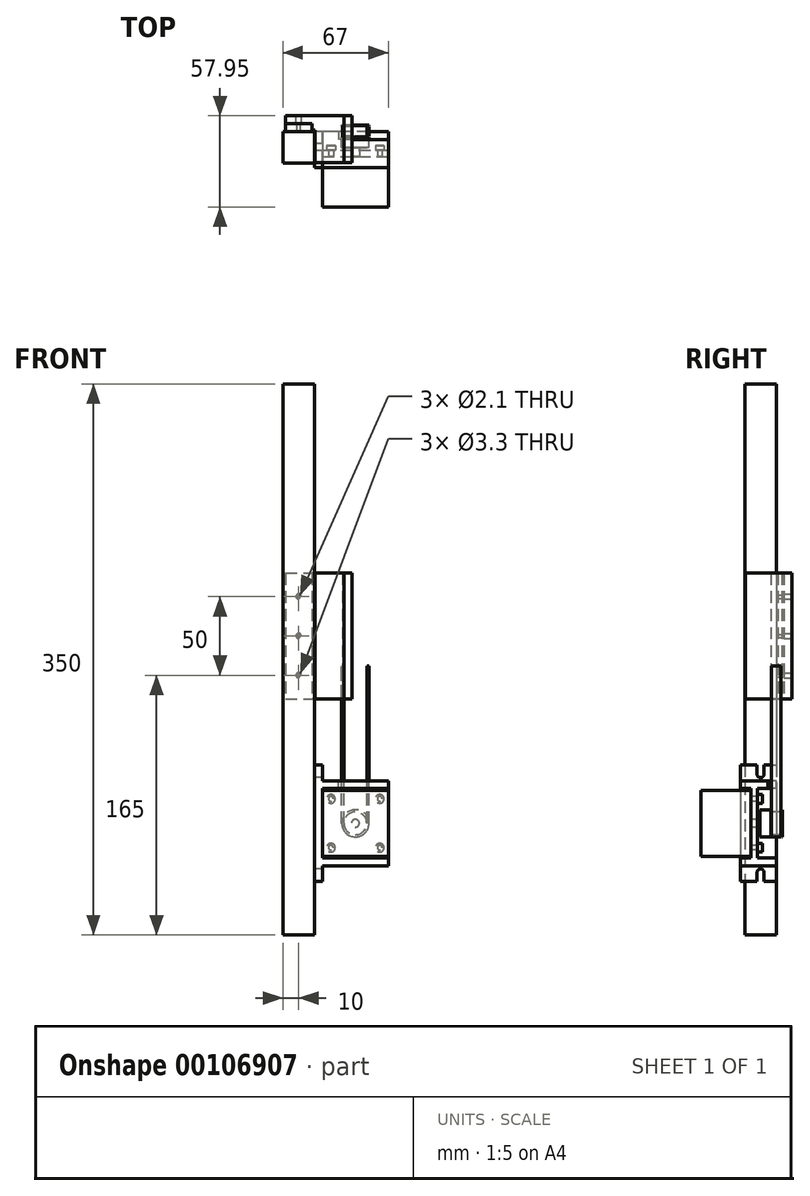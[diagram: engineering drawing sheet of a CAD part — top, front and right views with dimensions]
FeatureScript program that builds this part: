
annotation { "Feature Type Name" : "Feature", "Feature Type Description" : "" }
export const myFeature = defineFeature(function(context is Context, id is Id, definition is map)
    precondition{}
    {
        {
            var Q0;
            Q0=qCreatedBy(makeId("Top.planeOp"),FACE);
            var sketch = newSketch(context, id + "F0", { "sketchPlane" : qUnion([Q0])});
            skLineSegment(sketch, "E0.bottom", {"start": v(10, -10) * mm, "end": v(-10, -10) * mm, "construction": true});
            skLineSegment(sketch, "E0.top", {"start": v(10, 10) * mm, "end": v(-10, 10) * mm, "construction": true});
            skLineSegment(sketch, "E0.left", {"start": v(10, -10) * mm, "end": v(10, 10) * mm, "construction": true});
            skLineSegment(sketch, "E0.right", {"start": v(-10, -10) * mm, "end": v(-10, 10) * mm, "construction": true});
            skPoint(sketch, "E0.middle", {"position": v(0, 0) * mm});
            skLineSegment(sketch, "E1.bottom", {"start": v(15, -5.95) * mm, "end": v(57, -5.95) * mm, "construction": true});
            skLineSegment(sketch, "E1.top", {"start": v(15, -37.95) * mm, "end": v(57, -37.95) * mm, "construction": true});
            skLineSegment(sketch, "E1.left", {"start": v(15, -5.95) * mm, "end": v(15, -37.95) * mm, "construction": true});
            skLineSegment(sketch, "E1.right", {"start": v(57, -5.95) * mm, "end": v(57, -37.95) * mm, "construction": true});
            skLineSegment(sketch, "E2.bottom", {"start": v(33.5, -5.95) * mm, "end": v(38.5, -5.95) * mm, "construction": true});
            skLineSegment(sketch, "E2.top", {"start": v(33.5, 14.05) * mm, "end": v(38.5, 14.05) * mm, "construction": true});
            skLineSegment(sketch, "E2.left", {"start": v(33.5, -5.95) * mm, "end": v(33.5, 14.05) * mm, "construction": true});
            skLineSegment(sketch, "E2.right", {"start": v(38.5, -5.95) * mm, "end": v(38.5, 14.05) * mm, "construction": true});
            skPoint(sketch, "E2.middle", {"position": v(36, 4.05) * mm});
            skPoint(sketch, "E2.middle.positionSnap0", {"position": v(36, -5.95) * mm});
            skPoint(sketch, "E2.centerSnap0", {"position": v(36, -5.95) * mm});
            skLineSegment(sketch, "E3.top", {"start": v(44.65, -0.25) * mm, "end": v(27.35, -0.25) * mm, "construction": true});
            skLineSegment(sketch, "E3.left", {"start": v(44.65, 14.05) * mm, "end": v(44.65, -0.25) * mm, "construction": true});
            skPoint(sketch, "E3.middle", {"position": v(36, 6.9) * mm});
            skPoint(sketch, "E3.middle.positionSnap0", {"position": v(36, 14.05) * mm});
            skPoint(sketch, "E3.cornerSnap0", {"position": v(36, 14.05) * mm});
            skPoint(sketch, "E3.centerSnap0", {"position": v(36, 14.05) * mm});
            skLineSegment(sketch, "E4.bottom", {"start": v(-8.5, 10) * mm, "end": v(8.5, 10) * mm, "construction": true});
            skLineSegment(sketch, "E4.top", {"start": v(-8.5, 15) * mm, "end": v(8.5, 15) * mm, "construction": true});
            skLineSegment(sketch, "E4.left", {"start": v(-8.5, 10) * mm, "end": v(-8.5, 15) * mm, "construction": true});
            skLineSegment(sketch, "E4.right", {"start": v(8.5, 10) * mm, "end": v(8.5, 15) * mm, "construction": true});
            skPoint(sketch, "E4.middle", {"position": v(0, 12.5) * mm});
            skPoint(sketch, "E4.middle.positionSnap0", {"position": v(0, 10) * mm});
            skPoint(sketch, "E4.centerSnap0", {"position": v(0, 10) * mm});
            skLineSegment(sketch, "E5.bottom", {"start": v(10, 10) * mm, "end": v(15, 10) * mm, "construction": true});
            skLineSegment(sketch, "E5.top", {"start": v(10, -12.85) * mm, "end": v(15, -12.85) * mm, "construction": true});
            skLineSegment(sketch, "E5.left", {"start": v(10, 10) * mm, "end": v(10, -12.85) * mm, "construction": true});
            skLineSegment(sketch, "E5.right", {"start": v(15, 10) * mm, "end": v(15, -1.95) * mm, "construction": true});
            skLineSegment(sketch, "E6.bottom", {"start": v(15, -1.95) * mm, "end": v(57, -1.95) * mm, "construction": true});
            skLineSegment(sketch, "E6.right", {"start": v(57, -1.95) * mm, "end": v(57, -5.95) * mm, "construction": true});
            skLineSegment(sketch, "E7.trimOffspring", {"start": v(15, -5.95) * mm, "end": v(15, -12.85) * mm, "construction": true});
            skLineSegment(sketch, "E8", {"start": v(27.35, -0.25) * mm, "end": v(27.35, 14.05) * mm, "construction": true});
            skLineSegment(sketch, "E9", {"start": v(27.35, 14.05) * mm, "end": v(44.65, 14.05) * mm, "construction": true});
            skPoint(sketch, "E10", {"position": v(27.35, 6.9) * mm});
            skSolve(sketch);
        }
        {
            var Q0;
            Q0=qCreatedBy(makeId("Top.planeOp"),FACE);
            var sketch = newSketch(context, id + "F1", { "sketchPlane" : qUnion([Q0])});
            skLineSegment(sketch, "E11.0", {"start": v(10, -10) * mm, "end": v(-10, -10) * mm});
            skLineSegment(sketch, "E12.0", {"start": v(-10, -10) * mm, "end": v(-10, 10) * mm});
            skLineSegment(sketch, "E13.0", {"start": v(10, -10) * mm, "end": v(10, 10) * mm});
            skLineSegment(sketch, "E14.0", {"start": v(10, 10) * mm, "end": v(-10, 10) * mm});
            skSolve(sketch);
        }
        {
            var Q0;
            Q0 = qSketchRegion(id + "F1", true);
            extrude(context, id + "F2", {"entities" : qUnion([Q0]), "depth" : 300 * mm, "hasSecondDirection" : true, "secondDirectionOppositeDirection" : true, "secondDirectionDepth" : 50 * mm});
        }
        {
            var Q0;
            Q0=qCreatedBy(makeId("Top.planeOp"),FACE);
            var sketch = newSketch(context, id + "F3", { "sketchPlane" : qUnion([Q0])});
            skLineSegment(sketch, "E15.0", {"start": v(15, -5.95) * mm, "end": v(15, -37.95) * mm});
            skLineSegment(sketch, "E16.0", {"start": v(15, -5.95) * mm, "end": v(57, -5.95) * mm});
            skLineSegment(sketch, "E17.0", {"start": v(57, -5.95) * mm, "end": v(57, -37.95) * mm});
            skLineSegment(sketch, "E18.0", {"start": v(15, -37.95) * mm, "end": v(57, -37.95) * mm});
            skSolve(sketch);
        }
        {
            var Q0;
            Q0 = qSketchRegion(id + "F3", true);
            extrude(context, id + "F4", {"entities" : qUnion([Q0]), "depth" : 42 * mm});
        }
        {
            var Q0;
            Q0=makeQuery(id+"F4.opExtrude","SWEPT_FACE",FACE,{"disambiguationData":[OSD([sQuery(id+"F3.wireOp",EDGE,"E16.0")])]});
            var sketch = newSketch(context, id + "F5", { "sketchPlane" : qUnion([Q0])});
            skCircle(sketch, "E19", {"center": v(-36, 21) * mm, "radius": 2.5 * mm});
            skPoint(sketch, "E19.centerSnap0", {"position": v(-36, 42) * mm});
            skPoint(sketch, "E19.centerSnap1", {"position": v(-57, 21) * mm});
            skSolve(sketch);
        }
        {
            var Q0;
            Q0 = qSketchRegion(id + "F5", true);
            extrude(context, id + "F6", {"entities" : qUnion([Q0]), "operationType" : NewBodyOperationType.ADD, "depth" : 20 * mm});
        }
        {
            var Q0;
            Q0=makeQuery(id+"F6.opExtrude","CAP_FACE",FACE,{"disambiguationData":[OSD([sQuery(id+"F5.wireOp",EDGE,"E19")])],"isStart":false});
            var sketch = newSketch(context, id + "F7", { "sketchPlane" : qUnion([Q0])});
            skCircle(sketch, "E20", {"center": v(-36, 21) * mm, "radius": 8.65 * mm});
            skSolve(sketch);
        }
        {
            var Q0;
            Q0 = qSketchRegion(id + "F7", true);
            extrude(context, id + "F8", {"entities" : qUnion([Q0]), "operationType" : NewBodyOperationType.ADD, "oppositeDirection" : true, "depth" : 14.3 * mm});
        }
        {
            var Q0;
            Q0=makeQuery(id+"F4.opExtrude","SWEPT_FACE",FACE,{"disambiguationData":[OSD([sQuery(id+"F3.wireOp",EDGE,"E16.0")])]});
            var sketch = newSketch(context, id + "F9", { "sketchPlane" : qUnion([Q0])});
            skCircle(sketch, "E21.0", {"center": v(-36, 21) * mm, "radius": 2.5 * mm, "construction": true});
            skLineSegment(sketch, "E22.bottom", {"start": v(-20.5, 5.5) * mm, "end": v(-51.5, 5.5) * mm, "construction": true});
            skLineSegment(sketch, "E22.top", {"start": v(-20.5, 36.5) * mm, "end": v(-51.5, 36.5) * mm, "construction": true});
            skLineSegment(sketch, "E22.left", {"start": v(-20.5, 5.5) * mm, "end": v(-20.5, 36.5) * mm, "construction": true});
            skLineSegment(sketch, "E22.right", {"start": v(-51.5, 5.5) * mm, "end": v(-51.5, 36.5) * mm, "construction": true});
            skCircle(sketch, "E23", {"center": v(-51.5, 36.5) * mm, "radius": 1.5 * mm});
            skCircle(sketch, "E24.0.1.0", {"center": v(-51.5, 5.5) * mm, "radius": 1.5 * mm});
            skCircle(sketch, "E24.1.0.0", {"center": v(-20.5, 36.5) * mm, "radius": 1.5 * mm});
            skCircle(sketch, "E24.1.1.0", {"center": v(-20.5, 5.5) * mm, "radius": 1.5 * mm});
            skLineSegment(sketch, "E24.direction1", {"start": v(-51.5, 36.5) * mm, "end": v(-20.5, 36.5) * mm, "construction": true});
            skLineSegment(sketch, "E24.direction2", {"start": v(-51.5, 36.5) * mm, "end": v(-51.5, 5.5) * mm, "construction": true});
            skSolve(sketch);
        }
        {
            var Q0;
            Q0 = qSketchRegion(id + "F9", true);
            extrude(context, id + "F10", {"entities" : qUnion([Q0]), "operationType" : NewBodyOperationType.ADD, "depth" : 4 * mm});
        }
        {
            var Q0;
            Q0=makeQuery(id+"F10.opExtrude","CAP_FACE",FACE,{"disambiguationData":[OSD([sQuery(id+"F9.wireOp",EDGE,"E24.1.0.0")])],"isStart":false});
            var sketch = newSketch(context, id + "F11", { "sketchPlane" : qUnion([Q0])});
            skCircle(sketch, "E25", {"center": v(-20.5, 36.5) * mm, "radius": 2.75 * mm});
            skCircle(sketch, "E26.0.1.0", {"center": v(-20.5, 5.5) * mm, "radius": 2.75 * mm});
            skCircle(sketch, "E26.1.0.0", {"center": v(-51.5, 36.5) * mm, "radius": 2.75 * mm});
            skCircle(sketch, "E26.1.1.0", {"center": v(-51.5, 5.5) * mm, "radius": 2.75 * mm});
            skLineSegment(sketch, "E26.direction1", {"start": v(-20.5, 36.5) * mm, "end": v(-51.5, 36.5) * mm, "construction": true});
            skLineSegment(sketch, "E26.direction2", {"start": v(-20.5, 36.5) * mm, "end": v(-20.5, 5.5) * mm, "construction": true});
            skSolve(sketch);
        }
        {
            var Q0;
            Q0 = qSketchRegion(id + "F11", true);
            extrude(context, id + "F12", {"entities" : qUnion([Q0]), "operationType" : NewBodyOperationType.ADD, "depth" : 3 * mm});
        }
        {
            var Q0;
            Q0=qCreatedBy(makeId("Top.planeOp"),FACE);
            var sketch = newSketch(context, id + "F13", { "sketchPlane" : qUnion([Q0])});
            skLineSegment(sketch, "E27.0", {"start": v(15, -1.95) * mm, "end": v(57, -1.95) * mm});
            skLineSegment(sketch, "E28.0", {"start": v(57, -1.95) * mm, "end": v(57, -5.95) * mm});
            skLineSegment(sketch, "E29.0", {"start": v(15, -5.95) * mm, "end": v(57, -5.95) * mm});
            skLineSegment(sketch, "E30.0", {"start": v(15, 10) * mm, "end": v(15, -1.95) * mm});
            skLineSegment(sketch, "E31.0", {"start": v(10, 10) * mm, "end": v(15, 10) * mm});
            skLineSegment(sketch, "E32.0", {"start": v(10, 10) * mm, "end": v(10, -12.85) * mm});
            skLineSegment(sketch, "E33.0", {"start": v(10, -12.85) * mm, "end": v(15, -12.85) * mm});
            skLineSegment(sketch, "E34.0", {"start": v(15, 4.05) * mm, "end": v(15, -1.95) * mm});
            skLineSegment(sketch, "E35", {"start": v(15, -5.95) * mm, "end": v(15, -12.85) * mm});
            skSolve(sketch);
        }
        {
            var Q0;
            Q0 = qSketchRegion(id + "F13", true);
            extrude(context, id + "F14", {"entities" : qUnion([Q0]), "depth" : 43 * mm, "hasSecondDirection" : true, "secondDirectionOppositeDirection" : true, "secondDirectionDepth" : 1 * mm});
        }
        {
            var Q0;
            Q0=makeQuery(id+"F14.opExtrude","SWEPT_FACE",FACE,{"disambiguationData":[OSD([sQuery(id+"F13.wireOp",EDGE,"E32.0")])]});
            var sketch = newSketch(context, id + "F15", { "sketchPlane" : qUnion([Q0])});
            skLineSegment(sketch, "E36.bottom", {"start": v(12.85, 43) * mm, "end": v(-10, 43) * mm});
            skLineSegment(sketch, "E36.top", {"start": v(12.85, 58) * mm, "end": v(2.2, 58) * mm});
            skLineSegment(sketch, "E36.left", {"start": v(12.85, 43) * mm, "end": v(12.85, 58) * mm});
            skLineSegment(sketch, "E36.right", {"start": v(-10, 43) * mm, "end": v(-10, 58) * mm});
            skArc(sketch, "E37", {"start": v(-2.2, 52.2) * mm, "mid": v(0, 50) * mm, "end": v(2.2, 52.2) * mm});
            skPoint(sketch, "E37.centerSnap0", {"position": v(0, 58) * mm});
            skLineSegment(sketch, "E38", {"start": v(2.2, 52.2) * mm, "end": v(2.2, 58) * mm});
            skLineSegment(sketch, "E39", {"start": v(-2.2, 52.2) * mm, "end": v(-2.2, 58) * mm});
            skLineSegment(sketch, "E40.trimOffspring", {"start": v(-2.2, 58) * mm, "end": v(-10, 58) * mm});
            skPoint(sketch, "E41", {"position": v(0, 50) * mm});
            skLineSegment(sketch, "E42", {"start": v(-10, 21) * mm, "end": v(-15.85, 21) * mm, "construction": true});
            skLineSegment(sketch, "E43.MirrorCS", {"start": v(-2.2, -10.2) * mm, "end": v(-2.2, -16) * mm});
            skLineSegment(sketch, "E44.MirrorCS", {"start": v(-2.2, -16) * mm, "end": v(-10, -16) * mm});
            skArc(sketch, "E45.MirrorCS", {"start": v(-2.2, -10.2) * mm, "mid": v(0, -8) * mm, "end": v(2.2, -10.2) * mm});
            skLineSegment(sketch, "E46.MirrorCS", {"start": v(12.85, -1) * mm, "end": v(-10, -1) * mm});
            skLineSegment(sketch, "E47.MirrorCS", {"start": v(12.85, -16) * mm, "end": v(2.2, -16) * mm});
            skLineSegment(sketch, "E48.MirrorCS", {"start": v(2.2, -10.2) * mm, "end": v(2.2, -16) * mm});
            skPoint(sketch, "E49.MirrorP", {"position": v(0, -8) * mm});
            skLineSegment(sketch, "E50.MirrorCS", {"start": v(12.85, -1) * mm, "end": v(12.85, -16) * mm});
            skPoint(sketch, "E51.MirrorP", {"position": v(0, -16) * mm});
            skLineSegment(sketch, "E52.MirrorCS", {"start": v(-10, -1) * mm, "end": v(-10, -16) * mm});
            skSolve(sketch);
        }
        {
            var Q0;
            Q0 = qSketchRegion(id + "F15", true);
            var Q1;
            Q1=makeQuery(id+"F14.opExtrude","SWEPT_FACE",FACE,{"disambiguationData":[OSD([sQuery(id+"F13.wireOp",EDGE,"E30.0")])]});
            extrude(context, id + "F16", {"entities" : qUnion([Q0]), "operationType" : NewBodyOperationType.ADD, "endBound" : BoundingType.UP_TO_SURFACE, "oppositeDirection" : true, "endBoundEntityFace" : qUnion([Q1]), "depth" : 25 * mm});
        }
        {
            var Q0;
            {var subQ0=sQuery(id+"F13.wireOp",EDGE,"E30.0");Q0=makeQuery(id+"F16.boolean.opBoolean","MERGE",FACE,{"derivedFrom":[makeQuery(id+"F14.opExtrude","SWEPT_FACE",FACE,{"disambiguationData":[OSD([subQ0])]}),makeQuery(id+"F14.opExtrude","SWEPT_FACE",FACE,{"disambiguationData":[OSD([sQuery(id+"F13.wireOp",EDGE,"E34.0")])]}),makeQuery(id+"F16.opExtrude","CAP_FACE",FACE,{"disambiguationData":[OSD([subQ0]),ownerDisambiguation([makeQuery(id+"F16.opExtrude","SWEPT_BODY",BODY,{"disambiguationData":[OSD([sQuery(id+"F15.wireOp",EDGE,"E36.bottom"),sQuery(id+"F15.wireOp",EDGE,"E36.top"),sQuery(id+"F15.wireOp",EDGE,"E36.left"),sQuery(id+"F15.wireOp",EDGE,"E36.right"),sQuery(id+"F15.wireOp",EDGE,"E37"),sQuery(id+"F15.wireOp",EDGE,"E38"),sQuery(id+"F15.wireOp",EDGE,"E39"),sQuery(id+"F15.wireOp",EDGE,"E40.trimOffspring")])]})])],"isStart":false}),makeQuery(id+"F16.opExtrude","CAP_FACE",FACE,{"disambiguationData":[OSD([subQ0]),ownerDisambiguation([makeQuery(id+"F16.opExtrude","SWEPT_BODY",BODY,{"disambiguationData":[OSD([sQuery(id+"F15.wireOp",EDGE,"E43.MirrorCS"),sQuery(id+"F15.wireOp",EDGE,"E44.MirrorCS"),sQuery(id+"F15.wireOp",EDGE,"E45.MirrorCS"),sQuery(id+"F15.wireOp",EDGE,"E46.MirrorCS"),sQuery(id+"F15.wireOp",EDGE,"E47.MirrorCS"),sQuery(id+"F15.wireOp",EDGE,"E48.MirrorCS"),sQuery(id+"F15.wireOp",EDGE,"E50.MirrorCS"),sQuery(id+"F15.wireOp",EDGE,"E52.MirrorCS")])]})])],"isStart":false})]});}
            var sketch = newSketch(context, id + "F17", { "sketchPlane" : qUnion([Q0])});
            skLineSegment(sketch, "E53.bottom", {"start": v(10, 43) * mm, "end": v(-12.85, 43) * mm});
            skLineSegment(sketch, "E53.top", {"start": v(10, 48) * mm, "end": v(-12.85, 48) * mm});
            skLineSegment(sketch, "E53.left", {"start": v(10, 43) * mm, "end": v(10, 48) * mm});
            skLineSegment(sketch, "E53.right", {"start": v(-12.85, 43) * mm, "end": v(-12.85, 48) * mm});
            skLineSegment(sketch, "E54", {"start": v(10, 21) * mm, "end": v(15.88, 21) * mm, "construction": true});
            skPoint(sketch, "E54.endSnap0", {"position": v(10, 21) * mm});
            skLineSegment(sketch, "E55.MirrorCS", {"start": v(-12.85, -1) * mm, "end": v(-12.85, -6) * mm});
            skLineSegment(sketch, "E56.MirrorCS", {"start": v(10, -1) * mm, "end": v(10, -6) * mm});
            skLineSegment(sketch, "E57.MirrorCS", {"start": v(10, -6) * mm, "end": v(-12.85, -6) * mm});
            skLineSegment(sketch, "E58.MirrorCS", {"start": v(10, -1) * mm, "end": v(-12.85, -1) * mm});
            skSolve(sketch);
        }
        {
            var Q0;
            Q0 = qSketchRegion(id + "F17", true);
            var Q1;
            Q1 = qSketchRegion(id + "F19", true);
            var Q2;
            Q2=makeQuery(id+"F14.opExtrude","SWEPT_FACE",FACE,{"disambiguationData":[OSD([sQuery(id+"F13.wireOp",EDGE,"E28.0")])]});
            extrude(context, id + "F18", {"entities" : qUnion([Q0, Q1]), "operationType" : NewBodyOperationType.ADD, "endBound" : BoundingType.UP_TO_SURFACE, "endBoundEntityFace" : qUnion([Q2]), "depth" : 25 * mm});
        }
        {
            var Q0;
            Q0=makeQuery(id+"F18.opExtrude","SWEPT_FACE",FACE,{"disambiguationData":[OSD([sQuery(id+"F17.wireOp",EDGE,"E53.top")])]});
            var sketch = newSketch(context, id + "F19", { "sketchPlane" : qUnion([Q0])});
            skLineSegment(sketch, "E59.0", {"start": v(44.65, 14.05) * mm, "end": v(44.65, -0.25) * mm, "construction": true});
            skLineSegment(sketch, "E60.0", {"start": v(27.35, 14.05) * mm, "end": v(27.35, -0.25) * mm, "construction": true});
            skLineSegment(sketch, "E61", {"start": v(44.65, -0.25) * mm, "end": v(27.35, -0.25) * mm, "construction": true});
            skLineSegment(sketch, "E62", {"start": v(44.65, 14.05) * mm, "end": v(27.35, 14.05) * mm, "construction": true});
            skLineSegment(sketch, "E63.bottom", {"start": v(57, 10) * mm, "end": v(25.35, 10) * mm});
            skLineSegment(sketch, "E63.top", {"start": v(57, 4.75) * mm, "end": v(25.35, 4.75) * mm});
            skLineSegment(sketch, "E63.left", {"start": v(57, 10) * mm, "end": v(57, 4.75) * mm});
            skLineSegment(sketch, "E63.right", {"start": v(25.35, 10) * mm, "end": v(25.35, 4.75) * mm});
            skSolve(sketch);
        }
        {
            var Q0;
            Q0 = qSketchRegion(id + "F19", true);
            var Q1;
            {var subQ5=sQuery(id+"F17.wireOp",EDGE,"E53.bottom");Q1=makeQuery(id+"F18.boolean.opBoolean","SPLIT",FACE,{"disambiguationData":[TD([makeQuery(id+"F14.opExtrude","SWEPT_FACE",FACE,{"disambiguationData":[OSD([sQuery(id+"F13.wireOp",EDGE,"E27.0")])]})])],"derivedFrom":makeQuery(id+"F18.opExtrude","SWEPT_FACE",FACE,{"disambiguationData":[OSD([subQ5])]})});}
            extrude(context, id + "F20", {"entities" : qUnion([Q0]), "operationType" : NewBodyOperationType.REMOVE, "endBound" : BoundingType.UP_TO_SURFACE, "oppositeDirection" : true, "endBoundEntityFace" : qUnion([Q1]), "depth" : 25 * mm});
        }
        {
            var Q0;
            Q0=qCreatedBy(makeId("Top.planeOp"),FACE);
            cPlane(context, id + "F21", {"entities" : qUnion([Q0]), "cplaneType" : CPlaneType.OFFSET, "offset" : 100 * mm, "width" : 150 * mm, "height" : 150 * mm});
        }
        {
            var Q0;
            Q0=qCreatedBy(id+"F21.planeOp",FACE);
            var sketch = newSketch(context, id + "F22", { "sketchPlane" : qUnion([Q0])});
            skLineSegment(sketch, "E64.0", {"start": v(-8.5, 15) * mm, "end": v(8.5, 15) * mm});
            skLineSegment(sketch, "E65.0", {"start": v(-8.5, 10) * mm, "end": v(-8.5, 15) * mm});
            skLineSegment(sketch, "E66.0", {"start": v(-8.5, 10) * mm, "end": v(8.5, 10) * mm});
            skLineSegment(sketch, "E67.0", {"start": v(8.5, 10) * mm, "end": v(8.5, 15) * mm});
            skSolve(sketch);
        }
        {
            var Q0;
            Q0 = qSketchRegion(id + "F22", true);
            extrude(context, id + "F23", {"entities" : qUnion([Q0]), "depth" : 80 * mm});
        }
        {
            var Q0;
            Q0=makeQuery(id+"F23.opExtrude","SWEPT_FACE",FACE,{"disambiguationData":[OSD([sQuery(id+"F22.wireOp",EDGE,"E64.0")])]});
            var sketch = newSketch(context, id + "F24", { "sketchPlane" : qUnion([Q0])});
            skCircle(sketch, "E68", {"center": v(0, 165) * mm, "radius": 1.05 * mm});
            skCircle(sketch, "E69.0.1.0", {"center": v(0, 140) * mm, "radius": 1.05 * mm});
            skCircle(sketch, "E69.0.2.0", {"center": v(0, 115) * mm, "radius": 1.05 * mm});
            skLineSegment(sketch, "E69.direction1", {"start": v(0, 165) * mm, "end": v(25, 165) * mm, "construction": true});
            skLineSegment(sketch, "E69.direction2", {"start": v(0, 165) * mm, "end": v(0, 140) * mm, "construction": true});
            skSolve(sketch);
        }
        {
            var Q0;
            Q0 = qSketchRegion(id + "F24", true);
            extrude(context, id + "F25", {"entities" : qUnion([Q0]), "operationType" : NewBodyOperationType.REMOVE, "endBound" : BoundingType.UP_TO_NEXT, "oppositeDirection" : true, "depth" : 25 * mm});
        }
        {
            var Q0;
            Q0=makeQuery(id+"F8.boolean.opBoolean","MERGE",FACE,{"derivedFrom":[makeQuery(id+"F6.opExtrude","CAP_FACE",FACE,{"disambiguationData":[OSD([sQuery(id+"F5.wireOp",EDGE,"E19")])],"isStart":false}),makeQuery(id+"F8.opExtrude","CAP_FACE",FACE,{"disambiguationData":[OSD([sQuery(id+"F7.wireOp",EDGE,"E20")])],"isStart":true})]});
            cPlane(context, id + "F26", {"entities" : qUnion([Q0]), "cplaneType" : CPlaneType.OFFSET, "offset" : 4 * mm, "oppositeDirection" : true, "width" : 150 * mm, "height" : 150 * mm});
        }
        {
            var Q0;
            Q0=qCreatedBy(id+"F26.planeOp",FACE);
            var sketch = newSketch(context, id + "F27", { "sketchPlane" : qUnion([Q0])});
            skCircle(sketch, "E70.0", {"center": v(-36, 21) * mm, "radius": 8.65 * mm});
            skCircle(sketch, "E71", {"center": v(-36, 21) * mm, "radius": 7.27 * mm});
            skSolve(sketch);
        }
        {
            var Q0;
            Q0 = qSketchRegion(id + "F27", true);
            extrude(context, id + "F28", {"entities" : qUnion([Q0]), "operationType" : NewBodyOperationType.REMOVE, "depth" : 3.6 * mm, "hasSecondDirection" : true, "secondDirectionOppositeDirection" : true, "secondDirectionDepth" : 3.6 * mm});
        }
        {
            var Q0;
            Q0=qCreatedBy(id+"F26.planeOp",FACE);
            var sketch = newSketch(context, id + "F29", { "sketchPlane" : qUnion([Q0])});
            skArc(sketch, "E72.0", {"start": v(-44.65, 21) * mm, "mid": v(-36, 12.35) * mm, "end": v(-27.35, 21) * mm});
            skArc(sketch, "E73.0", {"start": v(-43.27, 21) * mm, "mid": v(-36, 13.73) * mm, "end": v(-28.73, 21) * mm});
            skLineSegment(sketch, "E74", {"start": v(-43.27, 21) * mm, "end": v(-28.73, 21) * mm, "construction": true});
            skLineSegment(sketch, "E75.top", {"start": v(-44.65, 121) * mm, "end": v(-43.27, 121) * mm});
            skLineSegment(sketch, "E75.left", {"start": v(-44.65, 21) * mm, "end": v(-44.65, 121) * mm});
            skLineSegment(sketch, "E75.right", {"start": v(-43.27, 21) * mm, "end": v(-43.27, 121) * mm});
            skLineSegment(sketch, "E76", {"start": v(-36, 21) * mm, "end": v(-36, 36.15) * mm, "construction": true});
            skLineSegment(sketch, "E77.MirrorCS", {"start": v(-28.73, 21) * mm, "end": v(-28.73, 121) * mm});
            skLineSegment(sketch, "E78.MirrorCS", {"start": v(-27.35, 21) * mm, "end": v(-27.35, 121) * mm});
            skLineSegment(sketch, "E79.MirrorCS", {"start": v(-27.35, 121) * mm, "end": v(-28.73, 121) * mm});
            skSolve(sketch);
        }
        {
            var Q0;
            Q0 = qSketchRegion(id + "F29", true);
            extrude(context, id + "F30", {"entities" : qUnion([Q0]), "depth" : 3 * mm, "hasSecondDirection" : true, "secondDirectionOppositeDirection" : true, "secondDirectionDepth" : 3 * mm});
        }
        {
            var Q0;
            Q0=qCreatedBy(id+"F21.planeOp",FACE);
            var sketch = newSketch(context, id + "F31", { "sketchPlane" : qUnion([Q0])});
            skLineSegment(sketch, "E80.0", {"start": v(8.5, 10) * mm, "end": v(8.5, 15) * mm, "construction": true});
            skLineSegment(sketch, "E81.0", {"start": v(10.5, 10) * mm, "end": v(10.5, 11) * mm, "construction": true});
            skLineSegment(sketch, "E82.bottom", {"start": v(-8.5, 15) * mm, "end": v(8.5, 15) * mm});
            skLineSegment(sketch, "E82.top", {"start": v(-8.5, 20) * mm, "end": v(28.73, 20) * mm});
            skLineSegment(sketch, "E82.left", {"start": v(-8.5, 15) * mm, "end": v(-8.5, 20) * mm});
            skLineSegment(sketch, "E83.left", {"start": v(31.5, 15) * mm, "end": v(31.5, 15) * mm});
            skLineSegment(sketch, "E83.right", {"start": v(10.5, 15) * mm, "end": v(10.5, 15) * mm});
            skLineSegment(sketch, "E84.top", {"start": v(28.73, -9.75) * mm, "end": v(10.5, -9.75) * mm});
            skLineSegment(sketch, "E84.right", {"start": v(10.5, 11) * mm, "end": v(10.5, -9.75) * mm});
            skLineSegment(sketch, "E85.top", {"start": v(10.5, 11) * mm, "end": v(8.5, 11) * mm});
            skLineSegment(sketch, "E85.right", {"start": v(8.5, 15) * mm, "end": v(8.5, 11) * mm});
            skLineSegment(sketch, "E86.0.0", {"start": v(27.35, 7.05) * mm, "end": v(28.73, 7.05) * mm, "construction": true});
            skLineSegment(sketch, "E86.0.1", {"start": v(28.73, 7.05) * mm, "end": v(28.73, 13.05) * mm, "construction": true});
            skLineSegment(sketch, "E86.0.2", {"start": v(28.73, 13.05) * mm, "end": v(27.35, 13.05) * mm, "construction": true});
            skLineSegment(sketch, "E86.0.3", {"start": v(27.35, 13.05) * mm, "end": v(27.35, 7.05) * mm, "construction": true});
            skLineSegment(sketch, "E87.0", {"start": v(28.73, 13.55) * mm, "end": v(27.98, 13.55) * mm});
            skLineSegment(sketch, "E88.0", {"start": v(27.98, 6.55) * mm, "end": v(28.73, 6.55) * mm});
            skLineSegment(sketch, "E89", {"start": v(27.98, 6.55) * mm, "end": v(27.98, 13.55) * mm});
            skLineSegment(sketch, "E90", {"start": v(28.73, 13.55) * mm, "end": v(28.73, 20) * mm});
            skLineSegment(sketch, "E91", {"start": v(28.73, 6.55) * mm, "end": v(28.73, -9.75) * mm});
            skSolve(sketch);
        }
        {
            var Q0;
            Q0 = qSketchRegion(id + "F31", true);
            extrude(context, id + "F32", {"entities" : qUnion([Q0]), "depth" : 80 * mm});
        }
        {
            var Q0;
            Q0=makeQuery(id+"F32.opExtrude","SWEPT_FACE",FACE,{"disambiguationData":[OSD([sQuery(id+"F31.wireOp",EDGE,"E82.top")])]});
            var sketch = newSketch(context, id + "F33", { "sketchPlane" : qUnion([Q0])});
            skCircle(sketch, "E92.0", {"center": v(0, 115) * mm, "radius": 1.05 * mm, "construction": true});
            skCircle(sketch, "E93.0", {"center": v(0, 140) * mm, "radius": 1.05 * mm, "construction": true});
            skCircle(sketch, "E94.0", {"center": v(0, 165) * mm, "radius": 1.05 * mm, "construction": true});
            skCircle(sketch, "E95", {"center": v(0, 165) * mm, "radius": 1.65 * mm});
            skCircle(sketch, "E96.0.1.0", {"center": v(0, 140) * mm, "radius": 1.65 * mm});
            skCircle(sketch, "E96.0.2.0", {"center": v(0, 115) * mm, "radius": 1.65 * mm});
            skLineSegment(sketch, "E96.direction1", {"start": v(0, 165) * mm, "end": v(25, 165) * mm, "construction": true});
            skLineSegment(sketch, "E96.direction2", {"start": v(0, 165) * mm, "end": v(0, 140) * mm, "construction": true});
            skSolve(sketch);
        }
        {
            var Q0;
            Q0 = qSketchRegion(id + "F33", true);
            extrude(context, id + "F34", {"entities" : qUnion([Q0]), "operationType" : NewBodyOperationType.REMOVE, "endBound" : BoundingType.UP_TO_NEXT, "oppositeDirection" : true, "depth" : 25 * mm});
        }
        {
            var Q0;
            Q0=makeQuery(id+"F32.opExtrude","SWEPT_FACE",FACE,{"disambiguationData":[OSD([sQuery(id+"F31.wireOp",EDGE,"E91")])]});
            cPlane(context, id + "F35", {"entities" : qUnion([Q0]), "cplaneType" : CPlaneType.OFFSET, "offset" : 0 * mm, "width" : 150 * mm, "height" : 150 * mm});
        }
        {
            var Q0;
            Q0=qCreatedBy(id+"F35.planeOp",FACE);
            var sketch = newSketch(context, id + "F36", { "sketchPlane" : qUnion([Q0])});
            skLineSegment(sketch, "E97.0", {"start": v(-9.75, 180) * mm, "end": v(-9.75, 100) * mm});
            skLineSegment(sketch, "E98.0", {"start": v(20, 180) * mm, "end": v(-9.75, 180) * mm});
            skLineSegment(sketch, "E99.0", {"start": v(20, 180) * mm, "end": v(20, 100) * mm});
            skPoint(sketch, "E100.orphan", {"position": v(6.55, 180) * mm});
            skPoint(sketch, "E101.0.end.orphan", {"position": v(-9.75, 100) * mm});
            skPoint(sketch, "E102.extension.end.orphan", {"position": v(6.55, 100) * mm});
            skLineSegment(sketch, "E103", {"start": v(-9.75, 100) * mm, "end": v(20, 100) * mm});
            skSolve(sketch);
        }
        {
            var Q0;
            Q0 = qSketchRegion(id + "F36", true);
            extrude(context, id + "F37", {"entities" : qUnion([Q0]), "depth" : 5 * mm});
        }
    });
